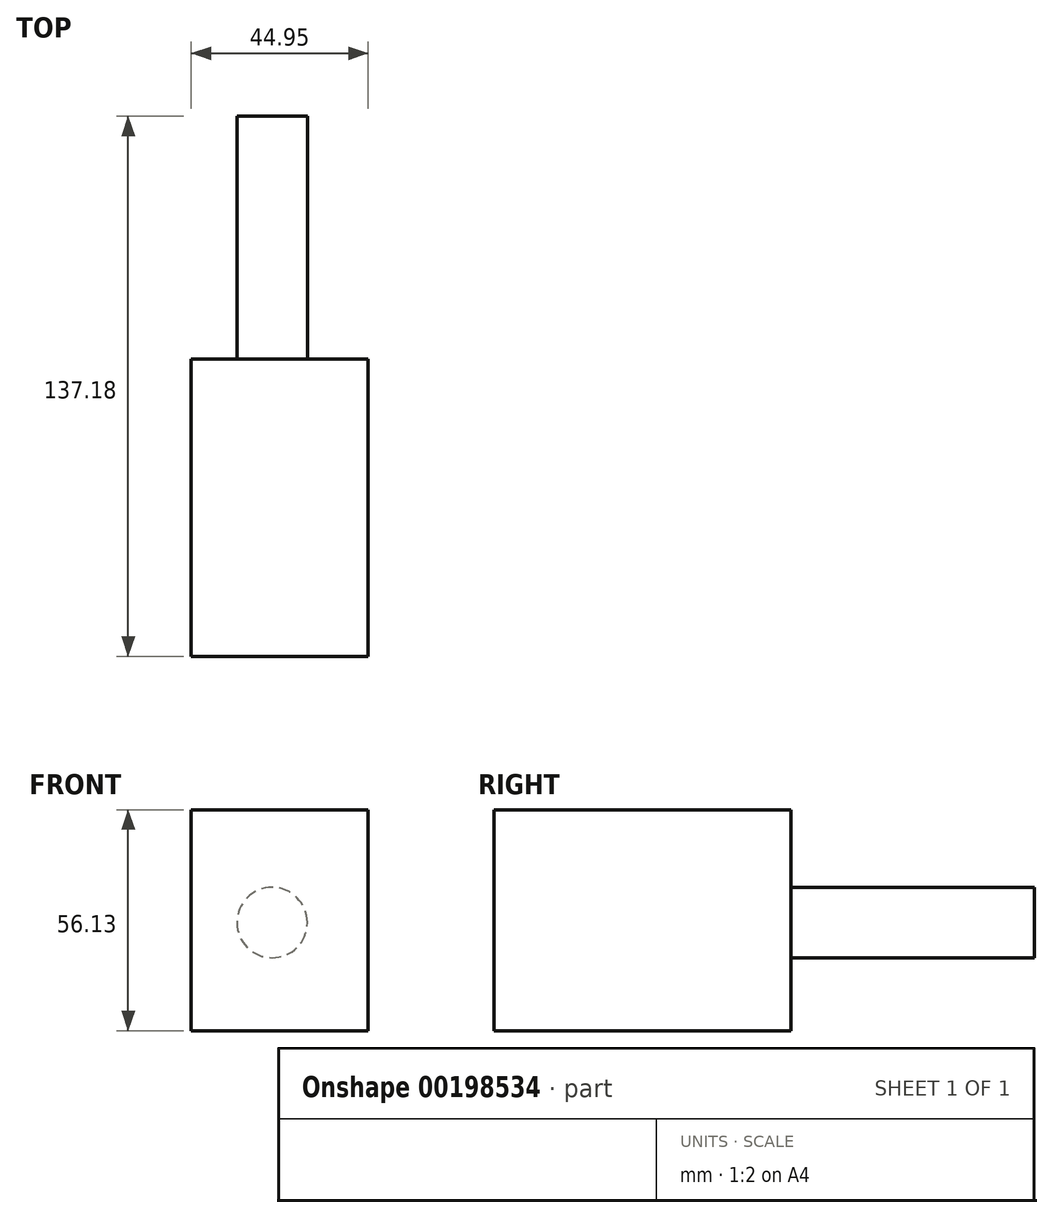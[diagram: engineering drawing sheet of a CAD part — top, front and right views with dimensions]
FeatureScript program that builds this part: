
annotation { "Feature Type Name" : "Feature", "Feature Type Description" : "" }
export const myFeature = defineFeature(function(context is Context, id is Id, definition is map)
    precondition{}
    {
        {
            var Q0;
            Q0=qCreatedBy(makeId("Top.planeOp"),FACE);
            var sketch = newSketch(context, id + "F0", { "sketchPlane" : qUnion([Q0])});
            skLineSegment(sketch, "E0.bottom", {"start": v(0, 0) * mm, "end": v(44.95, 0) * mm});
            skLineSegment(sketch, "E0.top", {"start": v(0, 75.46) * mm, "end": v(44.95, 75.46) * mm});
            skLineSegment(sketch, "E0.left", {"start": v(0, 0) * mm, "end": v(0, 75.46) * mm});
            skLineSegment(sketch, "E0.right", {"start": v(44.95, 0) * mm, "end": v(44.95, 75.46) * mm});
            skSolve(sketch);
        }
        {
            var Q0;
            Q0=makeQuery(id+"F0.imprint","IMPRINT",FACE,{"disambiguationData":[TD([[makeQuery(id+"F0.imprint","IMPRINT",EDGE,{"derivedFrom":sQuery(id+"F0.wireOp",EDGE,"E0.bottom")}),1.0]])]});
            extrude(context, id + "F1", {"entities" : qUnion([Q0]), "depth" : 56.13 * mm});
        }
        {
            var Q0;
            Q0=makeQuery(id+"F1.opExtrude","SWEPT_FACE",FACE,{"disambiguationData":[OSD([sQuery(id+"F0.wireOp",EDGE,"E0.top")])]});
            var sketch = newSketch(context, id + "F2", { "sketchPlane" : qUnion([Q0])});
            skCircle(sketch, "E1", {"center": v(-20.54, 27.46) * mm, "radius": 8.94 * mm});
            skSolve(sketch);
        }
        {
            var Q0;
            Q0 = qSketchRegion(id + "F2", true);
            extrude(context, id + "F3", {"entities" : qUnion([Q0]), "operationType" : NewBodyOperationType.ADD, "depth" : 61.72 * mm});
        }
    });
